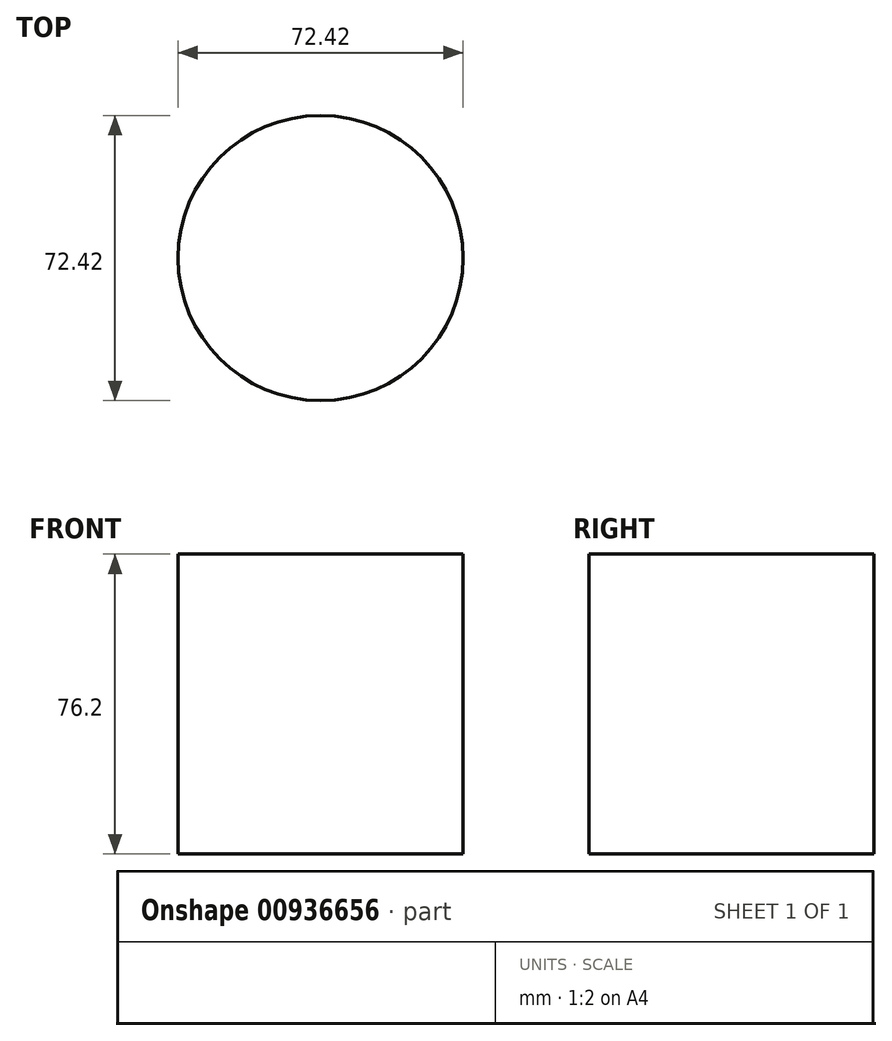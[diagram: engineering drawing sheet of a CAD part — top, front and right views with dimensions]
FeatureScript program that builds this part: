
annotation { "Feature Type Name" : "Feature", "Feature Type Description" : "" }
export const myFeature = defineFeature(function(context is Context, id is Id, definition is map)
    precondition{}
    {
        {
            var Q0;
            Q0=qCreatedBy(makeId("Top.planeOp"),FACE);
            var sketch = newSketch(context, id + "F0", { "sketchPlane" : qUnion([Q0])});
            skCircle(sketch, "E0", {"center": v(0, 0) * mm, "radius": 36.21 * mm});
            skSolve(sketch);
        }
        {
            var Q0;
            Q0 = qSketchRegion(id + "F0", true);
            extrude(context, id + "F1", {"entities" : qUnion([Q0]), "depth" : 76.2 * mm, "offsetDistance" : 25.4 * mm});
        }
    });
